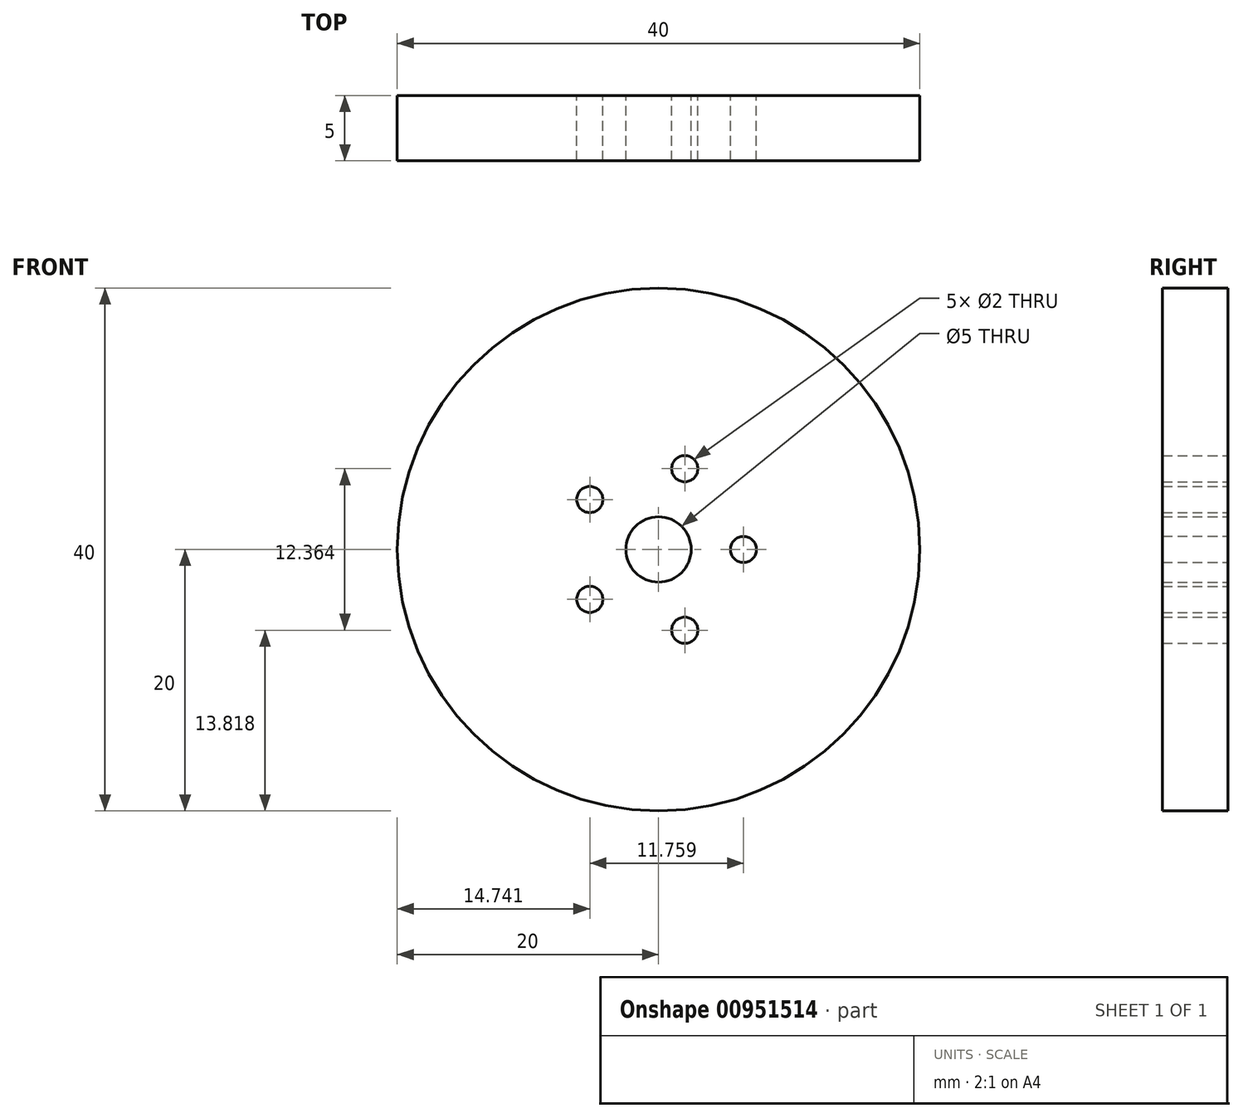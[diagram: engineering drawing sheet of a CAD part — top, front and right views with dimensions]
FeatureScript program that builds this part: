
annotation { "Feature Type Name" : "Feature", "Feature Type Description" : "" }
export const myFeature = defineFeature(function(context is Context, id is Id, definition is map)
    precondition{}
    {
        {
            var Q0;
            Q0=qCreatedBy(makeId("Front.planeOp"),FACE);
            var sketch = newSketch(context, id + "F0", { "sketchPlane" : qUnion([Q0])});
            skCircle(sketch, "E0", {"center": v(0, 0) * mm, "radius": 2.5 * mm});
            skCircle(sketch, "E1.cCircle", {"center": v(0, 0) * mm, "radius": 5.26 * mm, "construction": true});
            skLineSegment(sketch, "E1.0", {"start": v(-5.26, -3.82) * mm, "end": v(-5.26, 3.82) * mm});
            skLineSegment(sketch, "E1.1", {"start": v(-5.26, 3.82) * mm, "end": v(2, 6.18) * mm});
            skLineSegment(sketch, "E1.2", {"start": v(2, 6.18) * mm, "end": v(6.5, 0) * mm});
            skLineSegment(sketch, "E1.3", {"start": v(6.5, 0) * mm, "end": v(2, -6.18) * mm});
            skLineSegment(sketch, "E1.4", {"start": v(2, -6.18) * mm, "end": v(-5.26, -3.82) * mm});
            skPoint(sketch, "E1.0.midPoint", {"position": v(-5.26, 0) * mm});
            skCircle(sketch, "E2", {"center": v(-5.26, 3.82) * mm, "radius": 1 * mm});
            skCircle(sketch, "E3", {"center": v(2, 6.18) * mm, "radius": 1 * mm});
            skCircle(sketch, "E4", {"center": v(6.5, 0) * mm, "radius": 1 * mm});
            skCircle(sketch, "E5", {"center": v(2, -6.18) * mm, "radius": 1 * mm});
            skCircle(sketch, "E6", {"center": v(-5.26, -3.82) * mm, "radius": 1 * mm});
            skLineSegment(sketch, "E7", {"start": v(1.5, 2) * mm, "end": v(1.5, -2) * mm});
            skCircle(sketch, "E8", {"center": v(0, 0) * mm, "radius": 20 * mm});
            skSolve(sketch);
        }
        {
            var Q0;
            Q0 = qSketchRegion(id + "F0", true);
            var Q1;
            {var subQ20=sQuery(id+"F0.wireOp",EDGE,"E7");var subQ21=sQuery(id+"F0.wireOp",EDGE,"E0");var subQ22=makeQuery(id+"F0.imprint","INTERSECT",VERTEX,{"disambiguationData":[OD(0.0)],"derivedFrom":[subQ21,subQ20]});Q1=makeQuery(id+"F0.imprint","IMPRINT",FACE,{"disambiguationData":[TD([[makeQuery(id+"F0.imprint","IMPRINT",EDGE,{"disambiguationData":[TD([[subQ22,-1.0]])],"derivedFrom":subQ21}),-1.0]])]});}
            extrude(context, id + "F1", {"entities" : qUnion([Q0, Q1]), "depth" : 5 * mm, "offsetDistance" : 25 * mm});
        }
    });
